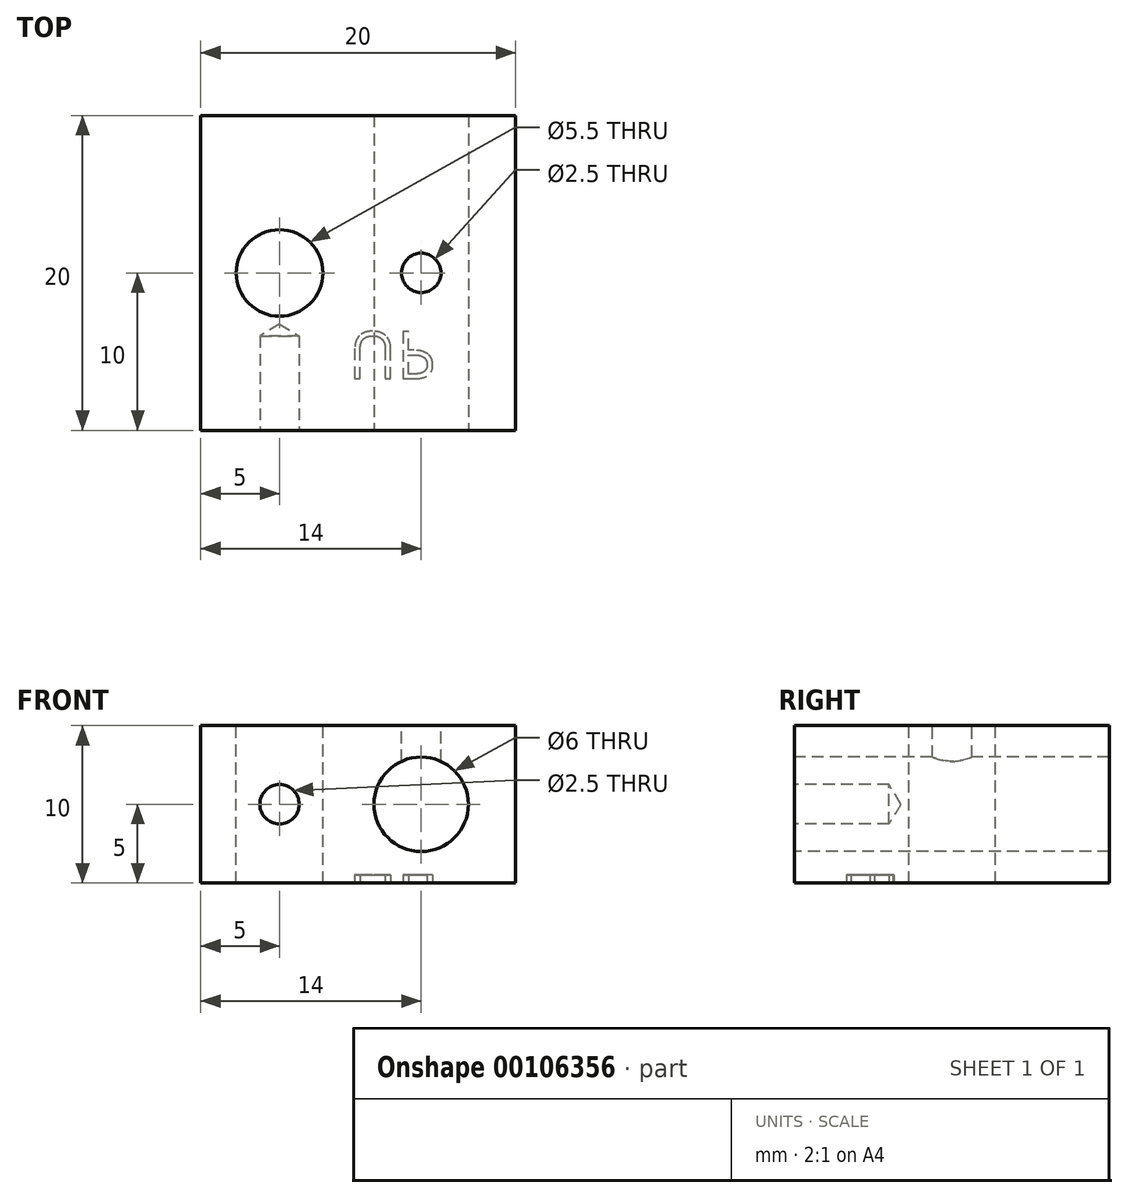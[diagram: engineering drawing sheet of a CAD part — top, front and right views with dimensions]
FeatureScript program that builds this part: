
annotation { "Feature Type Name" : "Feature", "Feature Type Description" : "" }
export const myFeature = defineFeature(function(context is Context, id is Id, definition is map)
    precondition{}
    {
        {
            var Q0;
            Q0=qCreatedBy(makeId("Top.planeOp"),FACE);
            var sketch = newSketch(context, id + "F0", { "sketchPlane" : qUnion([Q0])});
            skLineSegment(sketch, "E0.bottom", {"start": v(0, 0) * mm, "end": v(20, 0) * mm});
            skLineSegment(sketch, "E0.top", {"start": v(0, 20) * mm, "end": v(20, 20) * mm});
            skLineSegment(sketch, "E0.left", {"start": v(0, 0) * mm, "end": v(0, 20) * mm});
            skLineSegment(sketch, "E0.right", {"start": v(20, 0) * mm, "end": v(20, 20) * mm});
            skSolve(sketch);
        }
        {
            var Q0;
            Q0 = qSketchRegion(id + "F0", true);
            extrude(context, id + "F1", {"entities" : qUnion([Q0]), "depth" : 10 * mm});
        }
        {
            var Q0;
            Q0=makeQuery(id+"F1.opExtrude","SWEPT_FACE",FACE,{"disambiguationData":[OSD([sQuery(id+"F0.wireOp",EDGE,"E0.bottom")])]});
            var sketch = newSketch(context, id + "F2", { "sketchPlane" : qUnion([Q0])});
            skPoint(sketch, "E1", {"position": v(14, 5) * mm});
            skPoint(sketch, "E2", {"position": v(5, 5) * mm});
            skSolve(sketch);
        }
        {
            var Q0;
            Q0=sQuery(id+"F2.wireOp",VERTEX,"E1");
            var Q1;
            Q1=makeQuery(id+"F1.opExtrude","SWEPT_BODY",BODY,{"disambiguationData":[OSD([sQuery(id+"F0.wireOp",EDGE,"E0.bottom"),sQuery(id+"F0.wireOp",EDGE,"E0.top"),sQuery(id+"F0.wireOp",EDGE,"E0.left"),sQuery(id+"F0.wireOp",EDGE,"E0.right")])]});
            hole(context, id + "F3", {"style" : HoleStyle.SIMPLE, "endStyle" : HoleEndStyle.THROUGH, "holeDiameter" : 6 * mm, "locations" : qUnion([Q0]), "scope" : qUnion([Q1]), "isTappedThrough" : true});
        }
        {
            var Q0;
            Q0=sQuery(id+"F2.wireOp",VERTEX,"E2");
            var Q1;
            Q1=makeQuery(id+"F1.opExtrude","SWEPT_BODY",BODY,{"disambiguationData":[OSD([sQuery(id+"F0.wireOp",EDGE,"E0.bottom"),sQuery(id+"F0.wireOp",EDGE,"E0.top"),sQuery(id+"F0.wireOp",EDGE,"E0.left"),sQuery(id+"F0.wireOp",EDGE,"E0.right")])]});
            hole(context, id + "F4", {"style" : HoleStyle.SIMPLE, "endStyle" : HoleEndStyle.BLIND, "holeDiameter" : 2.5 * mm, "holeDepth" : 6 * mm, "locations" : qUnion([Q0]), "scope" : qUnion([Q1])});
        }
        {
            var Q0;
            Q0=makeQuery(id+"F1.opExtrude","CAP_FACE",FACE,{"disambiguationData":[OSD([sQuery(id+"F0.wireOp",EDGE,"E0.bottom"),sQuery(id+"F0.wireOp",EDGE,"E0.top"),sQuery(id+"F0.wireOp",EDGE,"E0.left"),sQuery(id+"F0.wireOp",EDGE,"E0.right")])],"isStart":false});
            var sketch = newSketch(context, id + "F5", { "sketchPlane" : qUnion([Q0])});
            skPoint(sketch, "E3", {"position": v(5, 10) * mm});
            skPoint(sketch, "E4", {"position": v(14, 10) * mm});
            skSolve(sketch);
        }
        {
            var Q0;
            Q0=sQuery(id+"F5.wireOp",VERTEX,"E3");
            var Q1;
            Q1=makeQuery(id+"F1.opExtrude","SWEPT_BODY",BODY,{"disambiguationData":[OSD([sQuery(id+"F0.wireOp",EDGE,"E0.bottom"),sQuery(id+"F0.wireOp",EDGE,"E0.top"),sQuery(id+"F0.wireOp",EDGE,"E0.left"),sQuery(id+"F0.wireOp",EDGE,"E0.right")])]});
            hole(context, id + "F6", {"style" : HoleStyle.SIMPLE, "endStyle" : HoleEndStyle.THROUGH, "holeDiameter" : 5.5 * mm, "locations" : qUnion([Q0]), "scope" : qUnion([Q1]), "isTappedThrough" : true});
        }
        {
            var Q0;
            Q0=sQuery(id+"F5.wireOp",VERTEX,"E4");
            var Q1;
            Q1=makeQuery(id+"F1.opExtrude","SWEPT_BODY",BODY,{"disambiguationData":[OSD([sQuery(id+"F0.wireOp",EDGE,"E0.bottom"),sQuery(id+"F0.wireOp",EDGE,"E0.top"),sQuery(id+"F0.wireOp",EDGE,"E0.left"),sQuery(id+"F0.wireOp",EDGE,"E0.right")])]});
            hole(context, id + "F7", {"style" : HoleStyle.SIMPLE, "endStyle" : HoleEndStyle.BLIND, "holeDiameter" : 2.5 * mm, "holeDepth" : 3 * mm, "locations" : qUnion([Q0]), "scope" : qUnion([Q1])});
        }
        {
            var Q0;
            Q0=makeQuery(id+"F1.opExtrude","CAP_FACE",FACE,{"disambiguationData":[OSD([sQuery(id+"F0.wireOp",EDGE,"E0.bottom"),sQuery(id+"F0.wireOp",EDGE,"E0.top"),sQuery(id+"F0.wireOp",EDGE,"E0.left"),sQuery(id+"F0.wireOp",EDGE,"E0.right")])],"isStart":true});
            var sketch = newSketch(context, id + "F8", { "sketchPlane" : qUnion([Q0])});
            skText(sketch, "E5", { "text": "UP", "fontName": "OpenSans-Regular.ttf"});
            const initialGuessF8  = {"E5": [0.0094, -0.00626, 1, 0, 0.003]};
            skSetInitialGuess(sketch, initialGuessF8);
            skSolve(sketch);
        }
        {
            var Q0;
            Q0 = qSketchRegion(id + "F8", true);
            extrude(context, id + "F9", {"entities" : qUnion([Q0]), "operationType" : NewBodyOperationType.REMOVE, "oppositeDirection" : true, "depth" : .5 * mm});
        }
    });
